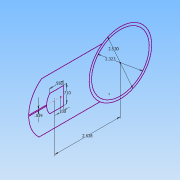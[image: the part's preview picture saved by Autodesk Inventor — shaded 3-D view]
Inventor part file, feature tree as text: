
AUTODESK INVENTOR PART (.ipt)
format: ipt  version: 2015 (Build 190159000, 159)  size: 73,216 bytes
history: native  units: in
note: dims shown in document units (in); Inventor stores cm internally (conversion verified against a paired STEP export)
features: sketch x1
ambient origin geometry x8: Origin, YZ Plane, XZ Plane, XY Plane, X Axis, Y Axis, Z Axis, Center Point
feature tree (1):
  sketch  "Sketch1"  dims[d0=0.71in d1=0.55in d2=0.1in d3=2.3228in d4=2.5197in d6=2.6378in d7=0.0394in]
